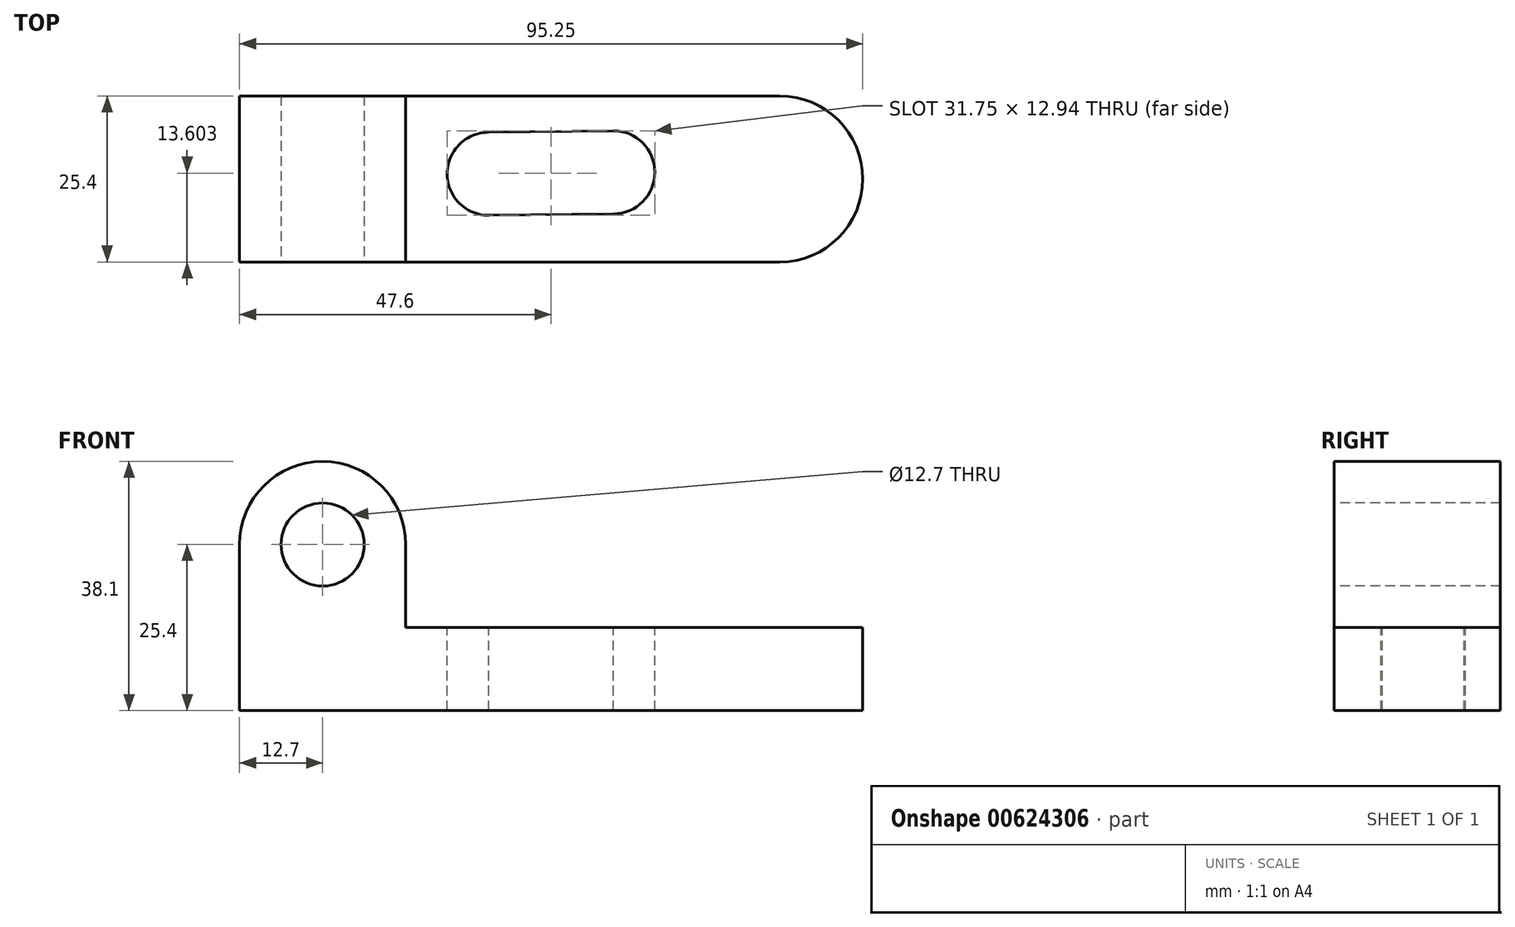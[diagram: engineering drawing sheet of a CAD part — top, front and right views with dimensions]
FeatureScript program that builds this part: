
annotation { "Feature Type Name" : "Feature", "Feature Type Description" : "" }
export const myFeature = defineFeature(function(context is Context, id is Id, definition is map)
    precondition{}
    {
        {
            var Q0;
            Q0=qCreatedBy(makeId("Front.planeOp"),FACE);
            var sketch = newSketch(context, id + "F0", { "sketchPlane" : qUnion([Q0])});
            skLineSegment(sketch, "E0", {"start": v(0, 0) * mm, "end": v(69.85, 0) * mm});
            skLineSegment(sketch, "E1", {"start": v(69.85, 0) * mm, "end": v(69.85, 38.1) * mm});
            skLineSegment(sketch, "E2", {"start": v(69.85, 38.1) * mm, "end": v(0, 38.1) * mm});
            skLineSegment(sketch, "E3", {"start": v(0, 38.1) * mm, "end": v(0, 0) * mm});
            skSolve(sketch);
        }
        {
            var Q0;
            Q0 = qSketchRegion(id + "F0", true);
            extrude(context, id + "F1", {"entities" : qUnion([Q0]), "depth" : 25.4 * mm, "offsetDistance" : 25.4 * mm});
        }
        {
            var Q0;
            Q0=makeQuery(id+"F1.opExtrude","CAP_FACE",FACE,{"disambiguationData":[OSD([sQuery(id+"F0.wireOp",EDGE,"E0"),sQuery(id+"F0.wireOp",EDGE,"E1"),sQuery(id+"F0.wireOp",EDGE,"E2"),sQuery(id+"F0.wireOp",EDGE,"E3")])],"isStart":false});
            var sketch = newSketch(context, id + "F2", { "sketchPlane" : qUnion([Q0])});
            skLineSegment(sketch, "E4", {"start": v(0, 0) * mm, "end": v(0, 25.4) * mm});
            skLineSegment(sketch, "E5", {"start": v(25.4, 25.4) * mm, "end": v(25.4, 12.7) * mm});
            skPoint(sketch, "E6.end.orphan", {"position": v(57.15, 0) * mm});
            skLineSegment(sketch, "E7", {"start": v(25.4, 12.7) * mm, "end": v(69.85, 12.7) * mm});
            skLineSegment(sketch, "E8", {"start": v(0, 0) * mm, "end": v(57.15, 0) * mm});
            skArc(sketch, "E9", {"start": v(25.4, 25.4) * mm, "mid": v(12.7, 38.1) * mm, "end": v(0, 25.4) * mm});
            skSolve(sketch);
        }
        {
            var Q0;
            {var subQ1=makeQuery(id+"F1.opExtrude","CAP_EDGE",EDGE,{"disambiguationData":[OSD([sQuery(id+"F0.wireOp",EDGE,"E3")])],"isStart":false});var subQ3=makeQuery(id+"F1.opExtrude","CAP_EDGE",EDGE,{"disambiguationData":[OSD([sQuery(id+"F0.wireOp",EDGE,"E2")])],"isStart":false});var subQ5=makeQuery(id+"F2.imprint","INTERSECT",VERTEX,{"derivedFrom":[subQ3,subQ1]});Q0=makeQuery(id+"F2.imprint","IMPRINT",FACE,{"disambiguationData":[TD([[makeQuery(id+"F2.imprint","IMPRINT",EDGE,{"disambiguationData":[TD([[subQ5,1.0]])],"derivedFrom":subQ3}),1.0]])]});}
            var Q1;
            {var subQ5=sQuery(id+"F2.wireOp",EDGE,"E5");Q1=makeQuery(id+"F2.imprint","IMPRINT",FACE,{"disambiguationData":[TD([[makeQuery(id+"F2.imprint","IMPRINT",EDGE,{"derivedFrom":subQ5}),1.0]])]});}
            extrude(context, id + "F3", {"entities" : qUnion([Q0, Q1]), "operationType" : NewBodyOperationType.REMOVE, "oppositeDirection" : true, "depth" : 25.4 * mm, "offsetDistance" : 25.4 * mm});
        }
        {
            var Q0;
            Q0=makeQuery(id+"F3.boolean.opBoolean","COPY",FACE,{"derivedFrom":makeQuery(id+"F3.opExtrude","SWEPT_FACE",FACE,{"disambiguationData":[OSD([sQuery(id+"F2.wireOp",EDGE,"E7")])]})});
            var sketch = newSketch(context, id + "F4", { "sketchPlane" : qUnion([Q0])});
            skArc(sketch, "E10", {"start": v(82.55, -25.4) * mm, "mid": v(95.25, -12.7) * mm, "end": v(82.55, 0) * mm});
            skLineSegment(sketch, "E11", {"start": v(69.85, 0) * mm, "end": v(82.55, 0) * mm});
            skLineSegment(sketch, "E12", {"start": v(69.85, -25.4) * mm, "end": v(82.55, -25.4) * mm});
            skLineSegment(sketch, "E13", {"start": v(69.85, 0) * mm, "end": v(69.85, -25.4) * mm});
            skSolve(sketch);
        }
        {
            var Q0;
            Q0 = qSketchRegion(id + "F4", true);
            extrude(context, id + "F5", {"entities" : qUnion([Q0]), "operationType" : NewBodyOperationType.ADD, "oppositeDirection" : true, "depth" : 12.7 * mm, "offsetDistance" : 25.4 * mm});
        }
        {
            var Q0;
            Q0=makeQuery(id+"F5.boolean.opBoolean","MERGE",FACE,{"derivedFrom":[makeQuery(id+"F3.boolean.opBoolean","COPY",FACE,{"derivedFrom":makeQuery(id+"F3.opExtrude","SWEPT_FACE",FACE,{"disambiguationData":[OSD([sQuery(id+"F2.wireOp",EDGE,"E7")])]})}),makeQuery(id+"F5.opExtrude","CAP_FACE",FACE,{"disambiguationData":[OSD([sQuery(id+"F4.wireOp",EDGE,"E10"),sQuery(id+"F4.wireOp",EDGE,"E11"),sQuery(id+"F4.wireOp",EDGE,"E12"),sQuery(id+"F4.wireOp",EDGE,"E13")])],"isStart":true})]});
            var sketch = newSketch(context, id + "F6", { "sketchPlane" : qUnion([Q0])});
            skCircle(sketch, "E14", {"center": v(38.08, -11.92) * mm, "radius": 6.35 * mm});
            skCircle(sketch, "E15", {"center": v(57.12, -11.68) * mm, "radius": 6.35 * mm});
            skLineSegment(sketch, "E16", {"start": v(38.08, -5.57) * mm, "end": v(57.12, -5.33) * mm});
            skLineSegment(sketch, "E17", {"start": v(57.12, -18.03) * mm, "end": v(38.08, -18.27) * mm});
            skSolve(sketch);
        }
        {
            var Q0;
            {var subQ0=sQuery(id+"F6.wireOp",EDGE,"E16");var subQ1=sQuery(id+"F6.wireOp",EDGE,"E14");var subQ2=makeQuery(id+"F6.imprint","INTERSECT",VERTEX,{"derivedFrom":[subQ1,subQ0]});Q0=makeQuery(id+"F6.imprint","IMPRINT",FACE,{"disambiguationData":[TD([[makeQuery(id+"F6.imprint","IMPRINT",EDGE,{"disambiguationData":[TD([[subQ2,1.0]])],"derivedFrom":subQ1}),-1.0]])]});}
            var Q1;
            {var subQ0=sQuery(id+"F6.wireOp",EDGE,"E15");var subQ1=makeQuery(id+"F6.imprint","INTERSECT",VERTEX,{"derivedFrom":[subQ0,sQuery(id+"F6.wireOp",EDGE,"E17")]});Q1=makeQuery(id+"F6.imprint","IMPRINT",FACE,{"disambiguationData":[TD([[makeQuery(id+"F6.imprint","IMPRINT",EDGE,{"disambiguationData":[TD([[subQ1,1.0]])],"derivedFrom":subQ0}),1.0]])]});}
            var Q2;
            {var subQ0=sQuery(id+"F6.wireOp",EDGE,"E14");var subQ1=makeQuery(id+"F6.imprint","INTERSECT",VERTEX,{"derivedFrom":[subQ0,sQuery(id+"F6.wireOp",EDGE,"E16")]});Q2=makeQuery(id+"F6.imprint","IMPRINT",FACE,{"disambiguationData":[TD([[makeQuery(id+"F6.imprint","IMPRINT",EDGE,{"disambiguationData":[TD([[subQ1,-1.0]])],"derivedFrom":subQ0}),1.0]])]});}
            extrude(context, id + "F7", {"entities" : qUnion([Q0, Q1, Q2]), "operationType" : NewBodyOperationType.REMOVE, "oppositeDirection" : true, "depth" : 25.4 * mm, "offsetDistance" : 25.4 * mm});
        }
        {
            var Q0;
            Q0=makeQuery(id+"F5.boolean.opBoolean","MERGE",FACE,{"derivedFrom":[makeQuery(id+"F1.opExtrude","CAP_FACE",FACE,{"disambiguationData":[OSD([sQuery(id+"F0.wireOp",EDGE,"E0"),sQuery(id+"F0.wireOp",EDGE,"E1"),sQuery(id+"F0.wireOp",EDGE,"E2"),sQuery(id+"F0.wireOp",EDGE,"E3")])],"isStart":false}),makeQuery(id+"F5.opExtrude","SWEPT_FACE",FACE,{"disambiguationData":[OSD([sQuery(id+"F4.wireOp",EDGE,"E12")])]})]});
            var sketch = newSketch(context, id + "F8", { "sketchPlane" : qUnion([Q0])});
            skCircle(sketch, "E18", {"center": v(12.7, 25.4) * mm, "radius": 6.35 * mm});
            skSolve(sketch);
        }
        {
            var Q0;
            Q0=makeQuery(id+"F8.imprint","IMPRINT",FACE,{"disambiguationData":[TD([[makeQuery(id+"F8.imprint","IMPRINT",EDGE,{"derivedFrom":sQuery(id+"F8.wireOp",EDGE,"E18")}),1.0]])]});
            extrude(context, id + "F9", {"entities" : qUnion([Q0]), "operationType" : NewBodyOperationType.REMOVE, "oppositeDirection" : true, "depth" : 25.4 * mm, "offsetDistance" : 25.4 * mm});
        }
    });
